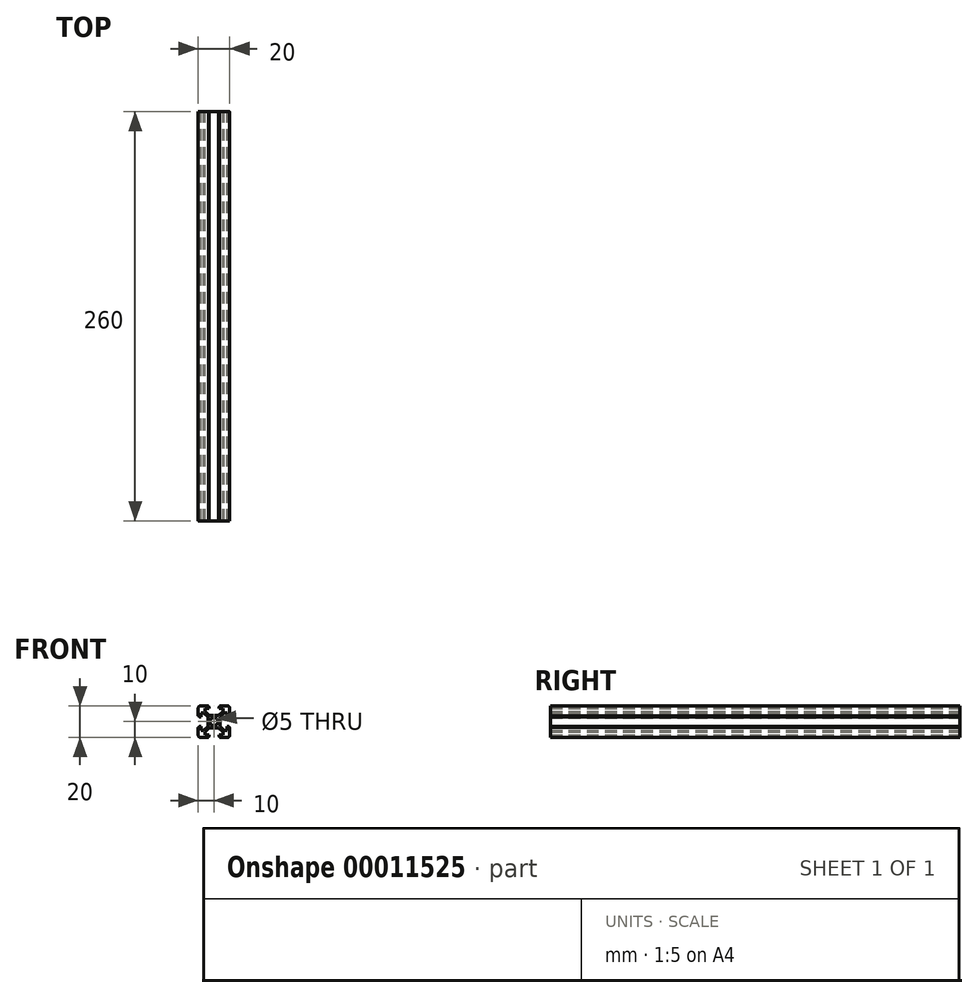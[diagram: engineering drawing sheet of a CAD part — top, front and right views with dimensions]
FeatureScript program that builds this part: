
annotation { "Feature Type Name" : "Feature", "Feature Type Description" : "" }
export const myFeature = defineFeature(function(context is Context, id is Id, definition is map)
    precondition{}
    {
        {
            var Q0;
            Q0=qCreatedBy(makeId("Front.planeOp"),FACE);
            var sketch = newSketch(context, id + "F0", { "sketchPlane" : qUnion([Q0])});
            skLineSegment(sketch, "E0", {"start": v(-10, 8.5) * mm, "end": v(-10, 3.6) * mm});
            skLineSegment(sketch, "E1", {"start": v(-10, 3.6) * mm, "end": v(-9.5, 3.6) * mm});
            skLineSegment(sketch, "E2", {"start": v(-9.5, 3.6) * mm, "end": v(-9.5, 3.1) * mm});
            skLineSegment(sketch, "E3", {"start": v(-9.5, 3.1) * mm, "end": v(-8.3, 3.1) * mm});
            skLineSegment(sketch, "E4", {"start": v(-8.3, 3.1) * mm, "end": v(-8.3, 5.63) * mm});
            skLineSegment(sketch, "E5", {"start": v(-8.3, 5.63) * mm, "end": v(-6.53, 5.63) * mm});
            skLineSegment(sketch, "E6", {"start": v(-6.53, 5.63) * mm, "end": v(-3.9, 3) * mm});
            skLineSegment(sketch, "E7", {"start": v(-8.5, 10) * mm, "end": v(-3.6, 10) * mm});
            skLineSegment(sketch, "E8", {"start": v(-3.6, 10) * mm, "end": v(-3.6, 9.5) * mm});
            skLineSegment(sketch, "E9", {"start": v(-3.6, 9.5) * mm, "end": v(-3.1, 9.5) * mm});
            skLineSegment(sketch, "E10", {"start": v(-3.1, 9.5) * mm, "end": v(-3.1, 8.3) * mm});
            skLineSegment(sketch, "E11", {"start": v(-3.1, 8.3) * mm, "end": v(-5.63, 8.3) * mm});
            skLineSegment(sketch, "E12", {"start": v(-5.63, 8.3) * mm, "end": v(-5.63, 6.53) * mm});
            skLineSegment(sketch, "E13", {"start": v(-5.63, 6.53) * mm, "end": v(-3, 3.9) * mm});
            skPoint(sketch, "E14.visualSharp", {"position": v(-10, 10) * mm});
            skArc(sketch, "E14.filletArc", {"start": v(-8.5, 10) * mm, "mid": v(-9.56, 9.56) * mm, "end": v(-10, 8.5) * mm});
            skLineSegment(sketch, "E15.0.MirrorCS", {"start": v(3.1, 9.5) * mm, "end": v(3.1, 8.3) * mm});
            skLineSegment(sketch, "E15.1.MirrorCS", {"start": v(3.6, 9.5) * mm, "end": v(3.1, 9.5) * mm});
            skLineSegment(sketch, "E15.2.MirrorCS", {"start": v(3.6, 10) * mm, "end": v(3.6, 9.5) * mm});
            skLineSegment(sketch, "E15.3.MirrorCS", {"start": v(3.1, 8.3) * mm, "end": v(5.63, 8.3) * mm});
            skLineSegment(sketch, "E15.4.MirrorCS", {"start": v(9.5, 3.6) * mm, "end": v(9.5, 3.1) * mm});
            skLineSegment(sketch, "E15.5.MirrorCS", {"start": v(10, 3.6) * mm, "end": v(9.5, 3.6) * mm});
            skLineSegment(sketch, "E15.6.MirrorCS", {"start": v(8.3, 3.1) * mm, "end": v(8.3, 5.63) * mm});
            skArc(sketch, "E15.7.MirrorCS", {"start": v(8.5, 10) * mm, "mid": v(9.56, 9.56) * mm, "end": v(10, 8.5) * mm});
            skLineSegment(sketch, "E15.8.MirrorCS", {"start": v(9.5, 3.1) * mm, "end": v(8.3, 3.1) * mm});
            skLineSegment(sketch, "E15.9.MirrorCS", {"start": v(5.63, 8.3) * mm, "end": v(5.63, 6.53) * mm});
            skLineSegment(sketch, "E15.10.MirrorCS", {"start": v(8.3, 5.63) * mm, "end": v(6.53, 5.63) * mm});
            skLineSegment(sketch, "E15.12.MirrorCS", {"start": v(8.5, 10) * mm, "end": v(3.6, 10) * mm});
            skLineSegment(sketch, "E15.13.MirrorCS", {"start": v(6.53, 5.63) * mm, "end": v(3.9, 3) * mm});
            skPoint(sketch, "E15.14.MirrorP", {"position": v(10, 10) * mm});
            skLineSegment(sketch, "E15.15.MirrorCS", {"start": v(10, 8.5) * mm, "end": v(10, 3.6) * mm});
            skLineSegment(sketch, "E15.17.MirrorCS", {"start": v(5.63, 6.53) * mm, "end": v(3, 3.9) * mm});
            skLineSegment(sketch, "E16.0.MirrorCS", {"start": v(-5.63, -8.3) * mm, "end": v(-5.63, -6.53) * mm});
            skLineSegment(sketch, "E16.1.MirrorCS", {"start": v(-3.1, -9.5) * mm, "end": v(-3.1, -8.3) * mm});
            skLineSegment(sketch, "E16.2.MirrorCS", {"start": v(-3.1, -8.3) * mm, "end": v(-5.63, -8.3) * mm});
            skLineSegment(sketch, "E16.3.MirrorCS", {"start": v(-10, -3.6) * mm, "end": v(-9.5, -3.6) * mm});
            skLineSegment(sketch, "E16.4.MirrorCS", {"start": v(-3.6, -10) * mm, "end": v(-3.6, -9.5) * mm});
            skLineSegment(sketch, "E16.5.MirrorCS", {"start": v(8.3, -3.1) * mm, "end": v(8.3, -5.63) * mm});
            skLineSegment(sketch, "E16.6.MirrorCS", {"start": v(8.3, -5.63) * mm, "end": v(6.53, -5.63) * mm});
            skLineSegment(sketch, "E16.7.MirrorCS", {"start": v(3.1, -9.5) * mm, "end": v(3.1, -8.3) * mm});
            skLineSegment(sketch, "E16.8.MirrorCS", {"start": v(10, -3.6) * mm, "end": v(9.5, -3.6) * mm});
            skLineSegment(sketch, "E16.9.MirrorCS", {"start": v(9.5, -3.1) * mm, "end": v(8.3, -3.1) * mm});
            skLineSegment(sketch, "E16.10.MirrorCS", {"start": v(-10, -8.5) * mm, "end": v(-10, -3.6) * mm});
            skLineSegment(sketch, "E16.11.MirrorCS", {"start": v(-5.63, -6.53) * mm, "end": v(-3, -3.9) * mm});
            skLineSegment(sketch, "E16.12.MirrorCS", {"start": v(3.1, -8.3) * mm, "end": v(5.63, -8.3) * mm});
            skLineSegment(sketch, "E16.14.MirrorCS", {"start": v(10, -8.5) * mm, "end": v(10, -3.6) * mm});
            skLineSegment(sketch, "E16.15.MirrorCS", {"start": v(3.6, -10) * mm, "end": v(3.6, -9.5) * mm});
            skLineSegment(sketch, "E16.17.MirrorCS", {"start": v(8.5, -10) * mm, "end": v(3.6, -10) * mm});
            skLineSegment(sketch, "E16.18.MirrorCS", {"start": v(5.63, -8.3) * mm, "end": v(5.63, -6.53) * mm});
            skArc(sketch, "E16.20.MirrorCS", {"start": v(-8.5, -10) * mm, "mid": v(-9.56, -9.56) * mm, "end": v(-10, -8.5) * mm});
            skLineSegment(sketch, "E16.21.MirrorCS", {"start": v(6.53, -5.63) * mm, "end": v(3.9, -3) * mm});
            skLineSegment(sketch, "E16.22.MirrorCS", {"start": v(5.63, -6.53) * mm, "end": v(3, -3.9) * mm});
            skLineSegment(sketch, "E16.23.MirrorCS", {"start": v(-6.53, -5.63) * mm, "end": v(-3.9, -3) * mm});
            skLineSegment(sketch, "E16.25.MirrorCS", {"start": v(-8.5, -10) * mm, "end": v(-3.6, -10) * mm});
            skLineSegment(sketch, "E16.26.MirrorCS", {"start": v(-8.3, -5.63) * mm, "end": v(-6.53, -5.63) * mm});
            skLineSegment(sketch, "E16.27.MirrorCS", {"start": v(-8.3, -3.1) * mm, "end": v(-8.3, -5.63) * mm});
            skLineSegment(sketch, "E16.28.MirrorCS", {"start": v(-9.5, -3.1) * mm, "end": v(-8.3, -3.1) * mm});
            skArc(sketch, "E16.29.MirrorCS", {"start": v(8.5, -10) * mm, "mid": v(9.56, -9.56) * mm, "end": v(10, -8.5) * mm});
            skPoint(sketch, "E16.30.MirrorP", {"position": v(10, -10) * mm});
            skPoint(sketch, "E16.31.MirrorP", {"position": v(-10, -10) * mm});
            skCircle(sketch, "E17", {"center": v(0, 0) * mm, "radius": 2.5 * mm});
            skLineSegment(sketch, "E18", {"start": v(-9.5, -3.6) * mm, "end": v(-9.5, -3.1) * mm});
            skLineSegment(sketch, "E19", {"start": v(-3.1, -9.5) * mm, "end": v(-3.6, -9.5) * mm});
            skLineSegment(sketch, "E20", {"start": v(3.1, -9.5) * mm, "end": v(3.6, -9.5) * mm});
            skLineSegment(sketch, "E21", {"start": v(9.5, -3.6) * mm, "end": v(9.5, -3.1) * mm});
            skLineSegment(sketch, "E22", {"start": v(-3, 3.9) * mm, "end": v(3, 3.9) * mm});
            skLineSegment(sketch, "E23", {"start": v(3.9, 3) * mm, "end": v(3.9, -3) * mm});
            skLineSegment(sketch, "E24", {"start": v(3, -3.9) * mm, "end": v(-3, -3.9) * mm});
            skLineSegment(sketch, "E25", {"start": v(-3.9, -3) * mm, "end": v(-3.9, 3) * mm});
            skSolve(sketch);
        }
        {
            var Q0;
            Q0=makeQuery(id+"F0.imprint","IMPRINT",FACE,{"disambiguationData":[TD([[makeQuery(id+"F0.imprint","IMPRINT",EDGE,{"derivedFrom":sQuery(id+"F0.wireOp",EDGE,"E0")}),1.0]])]});
            extrude(context, id + "F1", {"entities" : qUnion([Q0]), "endBound" : BoundingType.SYMMETRIC, "depth" : 260 * mm});
        }
    });
